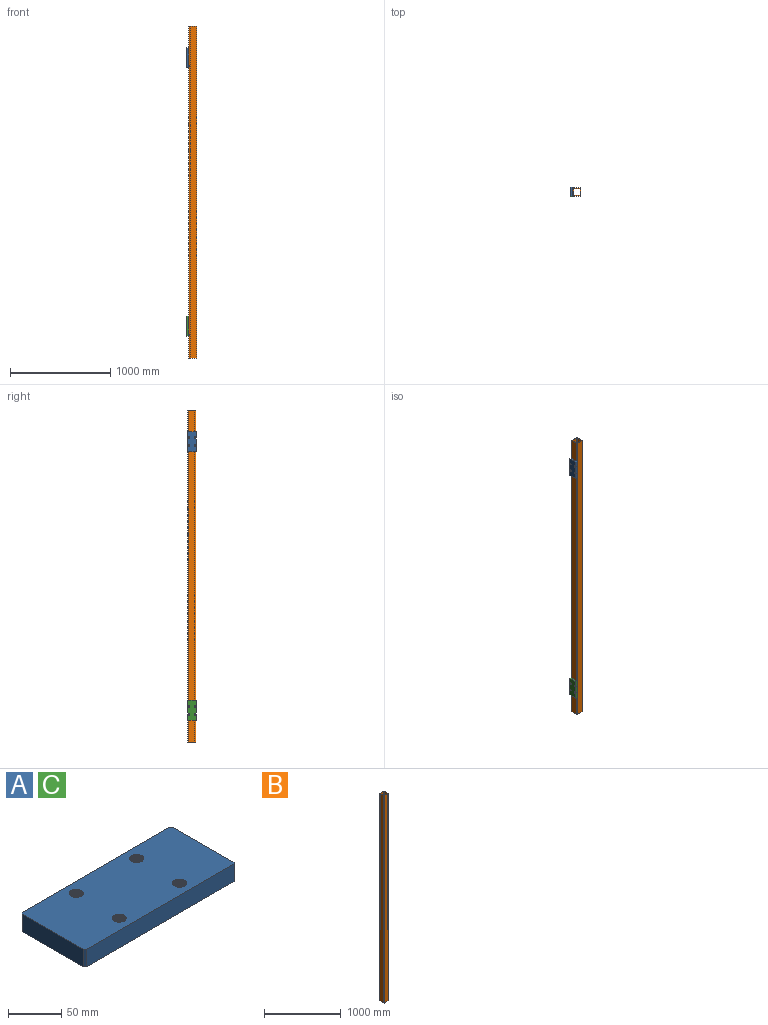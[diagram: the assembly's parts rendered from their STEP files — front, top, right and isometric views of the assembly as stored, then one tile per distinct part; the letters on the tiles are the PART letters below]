
ASSEMBLY  parts=3 mates=2
PART A: 26 faces, bbox 200.4x85.4x21 mm
  f0: plane 200.36x85.36mm, normal (0,0,-1), area 16429mm2, adj f1,f2,f3,f4,f5,f6,f8,f9
  f1: cylinder r=6.5mm len=20mm, axis (0,0,1), area 153.6mm2, adj f0,f7,f17,f18,f19
  f2: cylinder r=6.5mm len=20mm, axis (0,0,1), area 153.6mm2, adj f0,f7,f14,f15,f16
  f3: plane 196x20mm, normal (0,1,0), area 3920mm2, adj f0,f7,f10,f12
  f4: plane 81x20mm, normal (-1,0,0), area 1620mm2, adj f0,f7,f10,f13
  f5: plane 196x20mm, normal (0,-1,0), area 3920mm2, adj f0,f7,f11,f13
  f6: plane 81x20mm, normal (1,0,0), area 1620mm2, adj f0,f7,f11,f12
  f7: plane 200x85mm, normal (0,0,1), area 16461.1mm2, adj f1,f2,f3,f4,f5,f6,f8,f9
  f8: cylinder r=6.5mm len=20mm, axis (0,0,1), area 153.6mm2, adj f0,f7,f23,f24,f25
  f9: cylinder r=6.5mm len=20mm, axis (0,0,1), area 153.6mm2, adj f0,f7,f20,f21,f22
  f10: plane 20x2mm, normal (-0.71,0.71,0), area 56.6mm2, adj f0,f3,f4,f7
  f11: plane 20x2mm, normal (0.71,-0.71,0), area 56.6mm2, adj f0,f5,f6,f7
  f12: plane 20x2mm, normal (0.71,0.71,0), area 56.6mm2, adj f0,f3,f6,f7
  f13: plane 20x2mm, normal (-0.71,-0.71,0), area 56.6mm2, adj f0,f4,f5,f7
  f14: bspline ~20.43x16.51mm, area 441mm2, adj f0,f2,f15,f16
  f15: bspline ~20.18x16.51mm, area 441.3mm2, adj f0,f2,f14,f16
  f16: plane 0.87x0.75mm, normal (1,0,0), area 0.3mm2, adj f2,f14,f15
  f17: bspline ~20.43x16.51mm, area 441mm2, adj f0,f1,f18,f19
  f18: bspline ~20.18x16.51mm, area 441.3mm2, adj f0,f1,f17,f19
  f19: plane 0.87x0.75mm, normal (1,0,0), area 0.3mm2, adj f1,f17,f18
  f20: bspline ~20.43x16.51mm, area 437.1mm2, adj f0,f9,f21,f22
  f21: bspline ~20.18x16.51mm, area 438.9mm2, adj f0,f9,f20,f22
  f22: plane 0.87x0.75mm, normal (1,0,0), area 0.3mm2, adj f9,f20,f21
  f23: bspline ~20.43x16.51mm, area 437.1mm2, adj f0,f8,f24,f25
  f24: bspline ~20.18x16.51mm, area 438.9mm2, adj f0,f8,f23,f25
  f25: plane 0.87x0.75mm, normal (1,0,0), area 0.3mm2, adj f8,f23,f24
PART B: 18 faces, bbox 80x80x3320 mm
  f0: plane 80x80mm, normal (0,0,-1), area 1435.6mm2, adj f1,f2,f3,f4,f5,f6,f7,f8
  f1: plane 3320x60mm, normal (0,-1,0), area 199200mm2, adj f0,f2,f8,f17
  f2: cylinder r=5mm len=3320mm, axis (0,0,-1), area 26075.2mm2, adj f0,f1,f3,f17
  f3: plane 3320x60mm, normal (-1,0,0), area 199200mm2, adj f0,f2,f4,f17
  f4: cylinder r=5mm len=3320mm, axis (0,0,-1), area 26075.2mm2, adj f0,f3,f5,f17
  f5: plane 3320x60mm, normal (0,1,0), area 199200mm2, adj f0,f4,f6,f17
  f6: cylinder r=5mm len=3320mm, axis (0,0,-1), area 26075.2mm2, adj f0,f5,f7,f17
  f7: plane 3320x60mm, normal (1,0,0), area 199200mm2, adj f0,f6,f8,f17
  f8: cylinder r=5mm len=3320mm, axis (0,0,-1), area 26075.2mm2, adj f0,f1,f7,f17
  f9: cylinder r=10mm len=3320mm, axis (0,0,-1), area 52150.4mm2, adj f0,f10,f16,f17
  f10: plane 3320x60mm, normal (0,1,0), area 199200mm2, adj f0,f9,f11,f17
  f11: cylinder r=10mm len=3320mm, axis (0,0,-1), area 52150.4mm2, adj f0,f10,f12,f17
  f12: plane 3320x60mm, normal (-1,0,0), area 199200mm2, adj f0,f11,f13,f17
  f13: cylinder r=10mm len=3320mm, axis (0,0,-1), area 52150.4mm2, adj f0,f12,f14,f17
  f14: plane 3320x60mm, normal (0,-1,0), area 199200mm2, adj f0,f13,f15,f17
  f15: cylinder r=10mm len=3320mm, axis (0,0,-1), area 52150.4mm2, adj f0,f14,f16,f17
  f16: plane 3320x60mm, normal (1,0,0), area 199200mm2, adj f0,f9,f15,f17
  f17: plane 80x80mm, normal (0,0,1), area 1435.6mm2, adj f1,f2,f3,f4,f5,f6,f7,f8
PART C: same geometry as A
PLACE A rot(axis=(0.71,0,-0.71),180deg) t=(-983.54,-148.73,1967.15)mm
PLACE B t=(-983.54,-177.21,-38.68)mm
PLACE C rot(axis=(0.71,0,-0.71),180deg) t=(-983.54,-148.73,-720.85)mm
MATE fastened C.f0 <-> B.f12  axis (1,0,0) through (-983.54,-137.21,-732.68)mm
MATE fastened A.f0 <-> B.f12  axis (1,0,0) through (-983.54,-137.21,1955.32)mm
